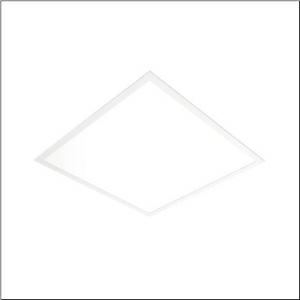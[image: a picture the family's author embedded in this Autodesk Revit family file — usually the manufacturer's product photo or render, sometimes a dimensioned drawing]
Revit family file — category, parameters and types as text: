
# Revit family: apollon_r__41_51mh12w72343_d43e
name_source: partatom
category: Lighting Fixtures
units: mm (PartAtom-declared; Revit-internal decimal feet)

## family parameters
Cut with Voids When Loaded = No
Host = Face
Light Source = No
Part Type = Normal
Room Calculation Point = No
Round Connector Dimension = Use Diameter
Shared = No

## types (1)
- Apollon® 41 (1 x LED, 3500 lm, 28.5 W, 3000K)
    Apparent Load = 29 VA
    CIE Flux Codes = 61 87 97 100 100
    Color Rendering = 80
    Color Temperature = 3000K
    Default Elevation = 1800 mm
    Description = Apollon® 41, office luminaire, primary optical cover: prismatic diffuser, of PS, light emission: direct distribution, primary light characteristic: symmetric, installation type: lay-in mounting, LED, rated luminous flux: 3.500lm, luminous efficacy: 123lm/W, light colour: 830, colour temperature: 3000K, control gear: ON/OFF, with terminal, 3-pole, mains connection: 220..240V, AC, 50/60Hz, housing, of aluminium section, traffic white (RAL 9016), module: M600, length: 595mm, width: 595mm, height: 60mm, recess depth: 180mm, housing upper side, of sheet steel, protection rating (complete): IP20, protection rating (lamp compartment, on room side): IP40, insulation class (complete): insulation class II (safety insulation), certification: CE, ENEC, impact resistance: IK03, permissible operating ambient temperature: -25..+40°C, packaging unit: 1 piece
    Height = 0 mm  [stored 0 ft]
    Lamp = 1 x LED
    Lamp Light Flux = 3500 lm
    Lamp Power = 28.5 W
    Lamp count = 1
    Length = 600 mm
    Luminous efficacy = 123 lm/W
    Manufacturer = Siteco
    ModVariant = No
    Model = 51MH12W72343
    Mounting Place = Ceiling
    Mounting Type = Recessed
    Number of Poles = 1
    OnlyDefault = Yes
    Power Factor = 1
    Product Name = Apollon® 41
    Product group = office luminaire | ceiling recessed
    ProductGroupID = 401
    Protection Class = Protection class II
    Protection Degree = IP 20
    RLX_Detail_Level = 1
    RLX_Emergency_Light_Flux = 0 lm
    RLX_Emergency_Type = 0
    RLX_Emergency_Type_DB = No
    RlxData = <blob elided: 12281 chars, md5=d458cd52>
    Socket = socket
    Standby Power = 0 W
    System Light Flux = 3500 lm
    System Power = 29 W
    Type Comments = Product without accessories
    Type Image = l_1291024.jpg
    URL = http://relux.com
    VarID = ---
    Voltage = 0 V
    Weight = 0.00 kg
    Width = 600 mm

note: [stored X ft] marks values corroborated as IEEE doubles in the binary element streams (Revit-internal decimal feet)

## geometry (parser evidence)
native form markers: Sweep x12
no freeform markers — native parametric forms only
